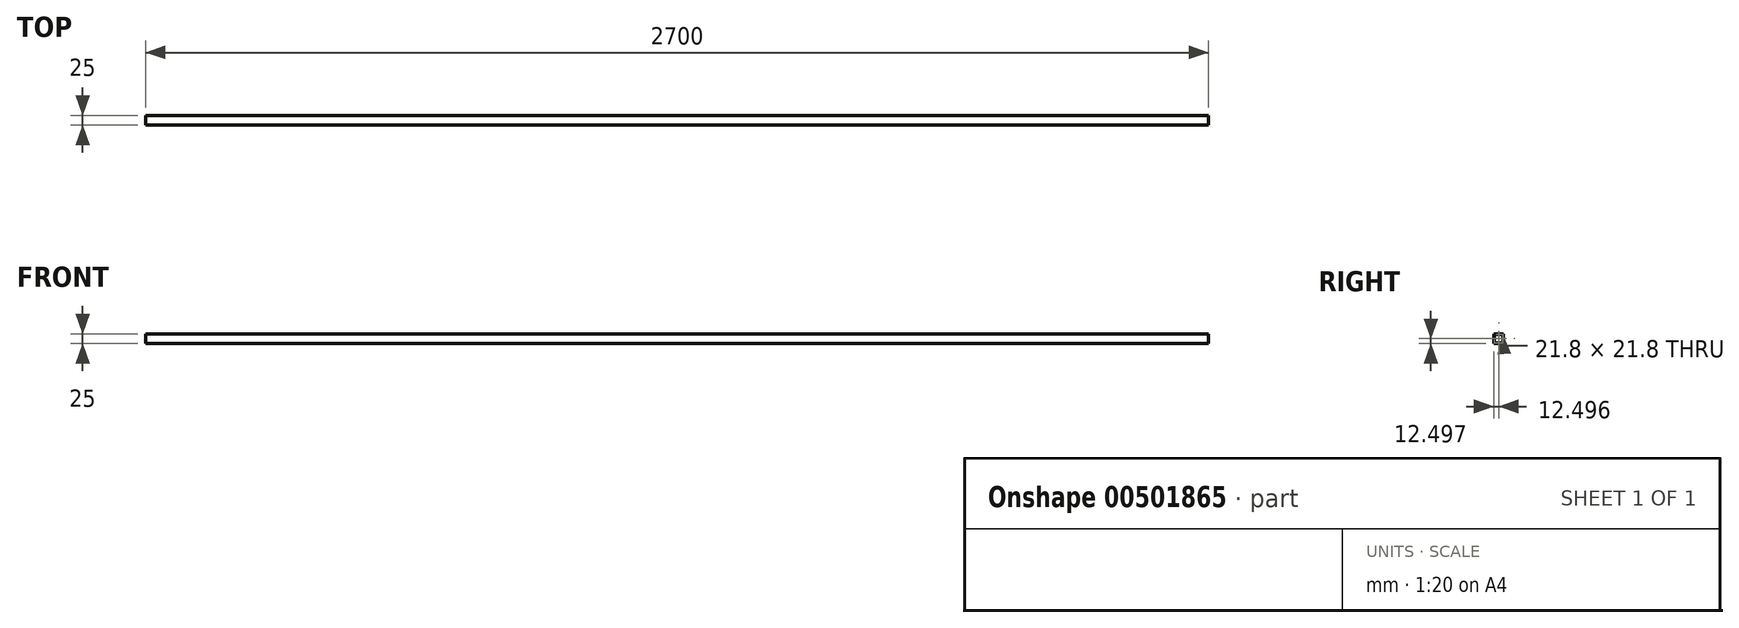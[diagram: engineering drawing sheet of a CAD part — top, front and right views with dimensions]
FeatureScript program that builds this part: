
annotation { "Feature Type Name" : "Feature", "Feature Type Description" : "" }
export const myFeature = defineFeature(function(context is Context, id is Id, definition is map)
    precondition{}
    {
        {
            var Q0;
            Q0=qCreatedBy(makeId("Right.planeOp"),FACE);
            var sketch = newSketch(context, id + "F0", { "sketchPlane" : qUnion([Q0])});
            skLineSegment(sketch, "E0.bottom", {"start": v(27.9, 44.77) * mm, "end": v(2.9, 44.77) * mm});
            skLineSegment(sketch, "E0.top", {"start": v(27.9, 19.77) * mm, "end": v(2.9, 19.77) * mm});
            skLineSegment(sketch, "E0.left", {"start": v(27.9, 44.77) * mm, "end": v(27.9, 19.77) * mm});
            skLineSegment(sketch, "E0.right", {"start": v(2.9, 44.77) * mm, "end": v(2.9, 19.77) * mm});
            skLineSegment(sketch, "E1.bottom", {"start": v(26.3, 43.17) * mm, "end": v(4.5, 43.17) * mm});
            skLineSegment(sketch, "E1.top", {"start": v(26.3, 21.37) * mm, "end": v(4.5, 21.37) * mm});
            skLineSegment(sketch, "E1.left", {"start": v(26.3, 43.17) * mm, "end": v(26.3, 21.37) * mm});
            skLineSegment(sketch, "E1.right", {"start": v(4.5, 43.17) * mm, "end": v(4.5, 21.37) * mm});
            skSolve(sketch);
        }
        {
            var Q0;
            Q0 = qSketchRegion(id + "F0", true);
            extrude(context, id + "F1", {"entities" : qUnion([Q0]), "depth" : 2700 * mm});
        }
    });
